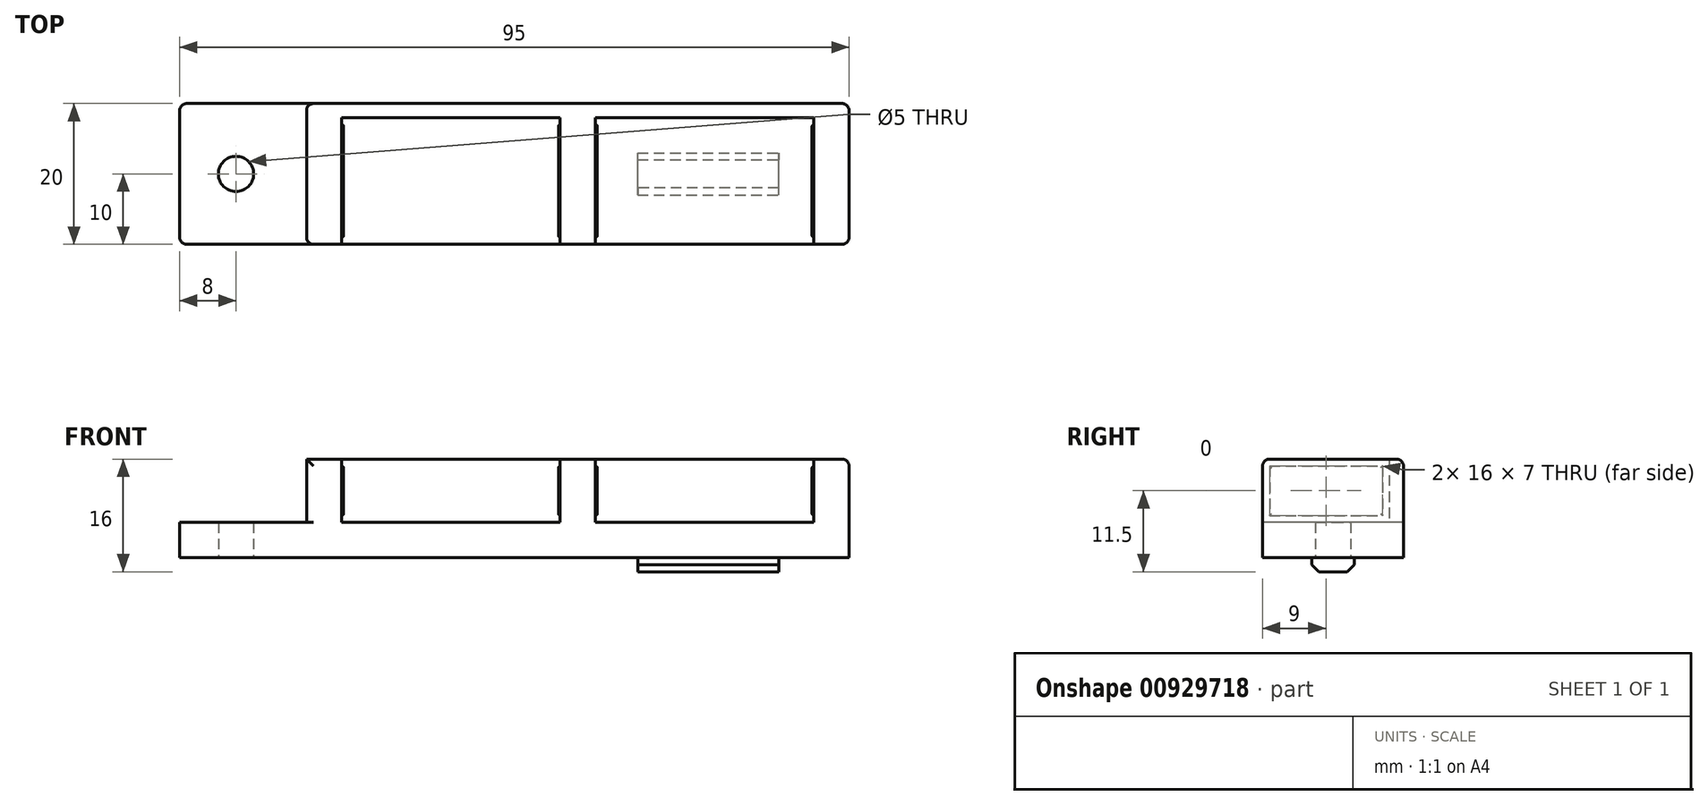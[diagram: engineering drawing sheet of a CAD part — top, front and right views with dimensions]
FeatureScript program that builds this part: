
annotation { "Feature Type Name" : "Feature", "Feature Type Description" : "" }
export const myFeature = defineFeature(function(context is Context, id is Id, definition is map)
    precondition{}
    {
        {
            var Q0;
            Q0=qCreatedBy(makeId("Top.planeOp"),FACE);
            var sketch = newSketch(context, id + "F0", { "sketchPlane" : qUnion([Q0])});
            skLineSegment(sketch, "E0.bottom", {"start": v(-47.5, 10) * mm, "end": v(47.5, 10) * mm});
            skLineSegment(sketch, "E0.top", {"start": v(-47.5, -10) * mm, "end": v(47.5, -10) * mm});
            skLineSegment(sketch, "E0.left", {"start": v(-47.5, 10) * mm, "end": v(-47.5, -10) * mm});
            skLineSegment(sketch, "E0.right", {"start": v(47.5, 10) * mm, "end": v(47.5, -10) * mm});
            skLineSegment(sketch, "E1.bottom", {"start": v(47.5, 10) * mm, "end": v(42.5, 10) * mm});
            skLineSegment(sketch, "E1.top", {"start": v(47.5, -10) * mm, "end": v(42.5, -10) * mm});
            skLineSegment(sketch, "E1.right", {"start": v(42.5, 10) * mm, "end": v(42.5, -10) * mm});
            skLineSegment(sketch, "E2.bottom", {"start": v(11.5, -10) * mm, "end": v(6.5, -10) * mm});
            skLineSegment(sketch, "E2.top", {"start": v(11.5, 10) * mm, "end": v(6.5, 10) * mm});
            skLineSegment(sketch, "E2.left", {"start": v(11.5, -10) * mm, "end": v(11.5, 10) * mm});
            skLineSegment(sketch, "E2.right", {"start": v(6.5, -10) * mm, "end": v(6.5, 10) * mm});
            skLineSegment(sketch, "E3.bottom", {"start": v(-29.5, 10) * mm, "end": v(-24.5, 10) * mm});
            skLineSegment(sketch, "E3.top", {"start": v(-29.5, -10) * mm, "end": v(-24.5, -10) * mm});
            skLineSegment(sketch, "E3.left", {"start": v(-29.5, 10) * mm, "end": v(-29.5, -10) * mm});
            skLineSegment(sketch, "E3.right", {"start": v(-24.5, 10) * mm, "end": v(-24.5, -10) * mm});
            skCircle(sketch, "E4", {"center": v(-39.5, 0) * mm, "radius": 2.5 * mm});
            skPoint(sketch, "E4.centerSnap0", {"position": v(-47.5, 0) * mm});
            skLineSegment(sketch, "E5.bottom", {"start": v(-24.5, 10) * mm, "end": v(6.5, 10) * mm});
            skLineSegment(sketch, "E5.top", {"start": v(-24.5, 8) * mm, "end": v(6.5, 8) * mm});
            skLineSegment(sketch, "E5.left", {"start": v(-24.5, 10) * mm, "end": v(-24.5, 8) * mm});
            skLineSegment(sketch, "E5.right", {"start": v(6.5, 10) * mm, "end": v(6.5, 8) * mm});
            skLineSegment(sketch, "E6.bottom", {"start": v(11.5, 10) * mm, "end": v(42.5, 10) * mm});
            skLineSegment(sketch, "E6.top", {"start": v(11.5, 8) * mm, "end": v(42.5, 8) * mm});
            skLineSegment(sketch, "E6.left", {"start": v(11.5, 10) * mm, "end": v(11.5, 8) * mm});
            skLineSegment(sketch, "E6.right", {"start": v(42.5, 10) * mm, "end": v(42.5, 8) * mm});
            skSolve(sketch);
        }
        {
            var Q0;
            {var subQ1=sQuery(id+"F0.wireOp",EDGE,"E0.left");Q0=makeQuery(id+"F0.imprint","IMPRINT",FACE,{"disambiguationData":[TD([[makeQuery(id+"F0.imprint","IMPRINT",EDGE,{"derivedFrom":subQ1}),1.0]])]});}
            var Q1;
            {var subQ4=sQuery(id+"F0.wireOp",EDGE,"E3.left");Q1=makeQuery(id+"F0.imprint","IMPRINT",FACE,{"disambiguationData":[TD([[makeQuery(id+"F0.imprint","IMPRINT",EDGE,{"derivedFrom":subQ4}),1.0]])]});}
            var Q2;
            {var subQ5=sQuery(id+"F0.wireOp",EDGE,"E5.top");Q2=makeQuery(id+"F0.imprint","IMPRINT",FACE,{"disambiguationData":[TD([[makeQuery(id+"F0.imprint","IMPRINT",EDGE,{"derivedFrom":subQ5}),-1.0]])]});}
            var Q3;
            {var subQ0=sQuery(id+"F0.wireOp",EDGE,"E2.left");var subQ1=sQuery(id+"F0.wireOp",EDGE,"E0.bottom");var subQ2=makeQuery(id+"F0.imprint","INTERSECT",VERTEX,{"derivedFrom":[subQ1,subQ0]});Q3=makeQuery(id+"F0.imprint","IMPRINT",FACE,{"disambiguationData":[TD([[makeQuery(id+"F0.imprint","IMPRINT",EDGE,{"disambiguationData":[TD([[subQ2,1.0]])],"derivedFrom":subQ1}),-1.0]])]});}
            var Q4;
            {var subQ4=sQuery(id+"F0.wireOp",EDGE,"E0.right");Q4=makeQuery(id+"F0.imprint","IMPRINT",FACE,{"disambiguationData":[TD([[makeQuery(id+"F0.imprint","IMPRINT",EDGE,{"derivedFrom":subQ4}),-1.0]])]});}
            var Q5;
            {var subQ5=sQuery(id+"F0.wireOp",EDGE,"E5.top");Q5=makeQuery(id+"F0.imprint","IMPRINT",FACE,{"disambiguationData":[TD([[makeQuery(id+"F0.imprint","IMPRINT",EDGE,{"derivedFrom":subQ5}),1.0]])]});}
            var Q6;
            {var subQ5=sQuery(id+"F0.wireOp",EDGE,"E6.top");Q6=makeQuery(id+"F0.imprint","IMPRINT",FACE,{"disambiguationData":[TD([[makeQuery(id+"F0.imprint","IMPRINT",EDGE,{"derivedFrom":subQ5}),-1.0]])]});}
            var Q7;
            {var subQ5=sQuery(id+"F0.wireOp",EDGE,"E6.top");Q7=makeQuery(id+"F0.imprint","IMPRINT",FACE,{"disambiguationData":[TD([[makeQuery(id+"F0.imprint","IMPRINT",EDGE,{"derivedFrom":subQ5}),1.0]])]});}
            extrude(context, id + "F1", {"entities" : qUnion([Q0, Q1, Q2, Q3, Q4, Q5, Q6, Q7]), "depth" : 5 * mm, "offsetDistance" : 25 * mm});
        }
        {
            var Q0;
            {var subQ4=sQuery(id+"F0.wireOp",EDGE,"E3.left");Q0=makeQuery(id+"F0.imprint","IMPRINT",FACE,{"disambiguationData":[TD([[makeQuery(id+"F0.imprint","IMPRINT",EDGE,{"derivedFrom":subQ4}),1.0]])]});}
            var Q1;
            {var subQ0=sQuery(id+"F0.wireOp",EDGE,"E2.left");var subQ1=sQuery(id+"F0.wireOp",EDGE,"E0.bottom");var subQ2=makeQuery(id+"F0.imprint","INTERSECT",VERTEX,{"derivedFrom":[subQ1,subQ0]});Q1=makeQuery(id+"F0.imprint","IMPRINT",FACE,{"disambiguationData":[TD([[makeQuery(id+"F0.imprint","IMPRINT",EDGE,{"disambiguationData":[TD([[subQ2,1.0]])],"derivedFrom":subQ1}),-1.0]])]});}
            var Q2;
            {var subQ4=sQuery(id+"F0.wireOp",EDGE,"E0.right");Q2=makeQuery(id+"F0.imprint","IMPRINT",FACE,{"disambiguationData":[TD([[makeQuery(id+"F0.imprint","IMPRINT",EDGE,{"derivedFrom":subQ4}),-1.0]])]});}
            var Q3;
            {var subQ5=sQuery(id+"F0.wireOp",EDGE,"E5.top");Q3=makeQuery(id+"F0.imprint","IMPRINT",FACE,{"disambiguationData":[TD([[makeQuery(id+"F0.imprint","IMPRINT",EDGE,{"derivedFrom":subQ5}),1.0]])]});}
            var Q4;
            {var subQ5=sQuery(id+"F0.wireOp",EDGE,"E6.top");Q4=makeQuery(id+"F0.imprint","IMPRINT",FACE,{"disambiguationData":[TD([[makeQuery(id+"F0.imprint","IMPRINT",EDGE,{"derivedFrom":subQ5}),1.0]])]});}
            extrude(context, id + "F2", {"entities" : qUnion([Q0, Q1, Q2, Q3, Q4]), "operationType" : NewBodyOperationType.ADD, "depth" : 14 * mm, "offsetDistance" : 25 * mm});
        }
        {
            var Q0;
            Q0=makeQuery(id+"F2.opExtrude","SWEPT_FACE",FACE,{"disambiguationData":[OSD([sQuery(id+"F0.wireOp",EDGE,"E3.right")])]});
            var sketch = newSketch(context, id + "F3", { "sketchPlane" : qUnion([Q0])});
            skLineSegment(sketch, "E7.bottom", {"start": v(-9, 13) * mm, "end": v(7, 13) * mm});
            skLineSegment(sketch, "E7.top", {"start": v(-9, 6) * mm, "end": v(7, 6) * mm});
            skLineSegment(sketch, "E7.left", {"start": v(-9, 13) * mm, "end": v(-9, 6) * mm});
            skLineSegment(sketch, "E7.right", {"start": v(7, 13) * mm, "end": v(7, 6) * mm});
            skSolve(sketch);
        }
        {
            var Q0;
            Q0=makeQuery(id+"F2.opExtrude","SWEPT_FACE",FACE,{"disambiguationData":[OSD([sQuery(id+"F0.wireOp",EDGE,"E2.right")])]});
            var sketch = newSketch(context, id + "F4", { "sketchPlane" : qUnion([Q0])});
            skLineSegment(sketch, "E8.bottom", {"start": v(-7, 6) * mm, "end": v(9, 6) * mm});
            skLineSegment(sketch, "E8.top", {"start": v(-7, 13) * mm, "end": v(9, 13) * mm});
            skLineSegment(sketch, "E8.left", {"start": v(-7, 6) * mm, "end": v(-7, 13) * mm});
            skLineSegment(sketch, "E8.right", {"start": v(9, 6) * mm, "end": v(9, 13) * mm});
            skSolve(sketch);
        }
        {
            var Q0;
            Q0=makeQuery(id+"F2.opExtrude","SWEPT_FACE",FACE,{"disambiguationData":[OSD([sQuery(id+"F0.wireOp",EDGE,"E2.left")])]});
            var sketch = newSketch(context, id + "F5", { "sketchPlane" : qUnion([Q0])});
            skLineSegment(sketch, "E9.bottom", {"start": v(-9, 13) * mm, "end": v(7, 13) * mm});
            skLineSegment(sketch, "E9.top", {"start": v(-9, 6) * mm, "end": v(7, 6) * mm});
            skLineSegment(sketch, "E9.left", {"start": v(-9, 13) * mm, "end": v(-9, 6) * mm});
            skLineSegment(sketch, "E9.right", {"start": v(7, 13) * mm, "end": v(7, 6) * mm});
            skSolve(sketch);
        }
        {
            var Q0;
            Q0=makeQuery(id+"F2.opExtrude","SWEPT_FACE",FACE,{"disambiguationData":[OSD([sQuery(id+"F0.wireOp",EDGE,"E1.right")])]});
            var sketch = newSketch(context, id + "F6", { "sketchPlane" : qUnion([Q0])});
            skLineSegment(sketch, "E10.bottom", {"start": v(-7, 13) * mm, "end": v(9, 13) * mm});
            skLineSegment(sketch, "E10.top", {"start": v(-7, 6) * mm, "end": v(9, 6) * mm});
            skLineSegment(sketch, "E10.left", {"start": v(-7, 13) * mm, "end": v(-7, 6) * mm});
            skLineSegment(sketch, "E10.right", {"start": v(9, 13) * mm, "end": v(9, 6) * mm});
            skSolve(sketch);
        }
        {
            var Q0;
            Q0=makeQuery(id+"F3.imprint","IMPRINT",FACE,{"disambiguationData":[TD([[makeQuery(id+"F3.imprint","IMPRINT",EDGE,{"derivedFrom":sQuery(id+"F3.wireOp",EDGE,"E7.bottom")}),-1.0]])]});
            var Q1;
            Q1=makeQuery(id+"F5.imprint","IMPRINT",FACE,{"disambiguationData":[TD([[makeQuery(id+"F5.imprint","IMPRINT",EDGE,{"derivedFrom":sQuery(id+"F5.wireOp",EDGE,"E9.bottom")}),-1.0]])]});
            extrude(context, id + "F7", {"entities" : qUnion([Q0, Q1]), "operationType" : NewBodyOperationType.ADD, "depth" : .25 * mm, "offsetDistance" : 25 * mm});
        }
        {
            var Q0;
            Q0=makeQuery(id+"F4.imprint","IMPRINT",FACE,{"disambiguationData":[TD([[makeQuery(id+"F4.imprint","IMPRINT",EDGE,{"derivedFrom":sQuery(id+"F4.wireOp",EDGE,"E8.bottom")}),1.0]])]});
            var Q1;
            Q1=makeQuery(id+"F6.imprint","IMPRINT",FACE,{"disambiguationData":[TD([[makeQuery(id+"F6.imprint","IMPRINT",EDGE,{"derivedFrom":sQuery(id+"F6.wireOp",EDGE,"E10.bottom")}),-1.0]])]});
            extrude(context, id + "F8", {"entities" : qUnion([Q0, Q1]), "operationType" : NewBodyOperationType.ADD, "depth" : .25 * mm, "offsetDistance" : 25 * mm});
        }
        {
            var Q0;
            Q0=makeQuery(id+"F7.opExtrude","CAP_FACE",FACE,{"disambiguationData":[OSD([sQuery(id+"F3.wireOp",EDGE,"E7.bottom"),sQuery(id+"F3.wireOp",EDGE,"E7.top"),sQuery(id+"F3.wireOp",EDGE,"E7.left"),sQuery(id+"F3.wireOp",EDGE,"E7.right")])],"isStart":false});
            var Q1;
            Q1=makeQuery(id+"F8.opExtrude","CAP_FACE",FACE,{"disambiguationData":[OSD([sQuery(id+"F4.wireOp",EDGE,"E8.bottom"),sQuery(id+"F4.wireOp",EDGE,"E8.top"),sQuery(id+"F4.wireOp",EDGE,"E8.left"),sQuery(id+"F4.wireOp",EDGE,"E8.right")])],"isStart":false});
            var Q2;
            Q2=makeQuery(id+"F7.opExtrude","CAP_FACE",FACE,{"disambiguationData":[OSD([sQuery(id+"F5.wireOp",EDGE,"E9.bottom"),sQuery(id+"F5.wireOp",EDGE,"E9.top"),sQuery(id+"F5.wireOp",EDGE,"E9.left"),sQuery(id+"F5.wireOp",EDGE,"E9.right")])],"isStart":false});
            var Q3;
            Q3=makeQuery(id+"F8.opExtrude","CAP_FACE",FACE,{"disambiguationData":[OSD([sQuery(id+"F6.wireOp",EDGE,"E10.bottom"),sQuery(id+"F6.wireOp",EDGE,"E10.top"),sQuery(id+"F6.wireOp",EDGE,"E10.left"),sQuery(id+"F6.wireOp",EDGE,"E10.right")])],"isStart":false});
            fillet(context, id + "F9", {"entities" : qUnion([Q0, Q1, Q2, Q3]), "radius" : .25 * mm, "tangentPropagation" : true, "allowEdgeOverflow" : false});
        }
        {
            var Q0;
            {var subQ0=sQuery(id+"F0.wireOp",EDGE,"E0.top");Q0=makeQuery(id+"F2.opExtrude","CAP_EDGE",EDGE,{"disambiguationData":[OSD([subQ0]),TDD([makeQuery(id+"F0.imprint","IMPRINT",EDGE,{"disambiguationData":[TD([[makeQuery(id+"F0.imprint","INTERSECT",VERTEX,{"derivedFrom":[subQ0,sQuery(id+"F0.wireOp",EDGE,"E3.right")]}),1.0]])],"derivedFrom":subQ0})])],"isStart":false});}
            var Q1;
            {var subQ0=sQuery(id+"F0.wireOp",EDGE,"E0.top");Q1=makeQuery(id+"F2.opExtrude","CAP_EDGE",EDGE,{"disambiguationData":[OSD([subQ0]),TDD([makeQuery(id+"F0.imprint","IMPRINT",EDGE,{"disambiguationData":[TD([[makeQuery(id+"F0.imprint","INTERSECT",VERTEX,{"derivedFrom":[subQ0,sQuery(id+"F0.wireOp",EDGE,"E2.left")]}),1.0]])],"derivedFrom":subQ0})])],"isStart":false});}
            var Q2;
            {var subQ0=sQuery(id+"F0.wireOp",EDGE,"E0.top");Q2=makeQuery(id+"F2.opExtrude","CAP_EDGE",EDGE,{"disambiguationData":[OSD([subQ0]),TDD([makeQuery(id+"F0.imprint","IMPRINT",EDGE,{"disambiguationData":[TD([[makeQuery(id+"F0.imprint","INTERSECT",VERTEX,{"derivedFrom":[subQ0,sQuery(id+"F0.wireOp",EDGE,"E0.right")]}),1.0]])],"derivedFrom":subQ0})])],"isStart":false});}
            var Q3;
            Q3=makeQuery(id+"F2.opExtrude","CAP_EDGE",EDGE,{"disambiguationData":[OSD([sQuery(id+"F0.wireOp",EDGE,"E0.bottom")])],"isStart":false});
            var Q4;
            Q4=makeQuery(id+"F1.opExtrude","SWEPT_EDGE",EDGE,{"disambiguationData":[OSD([sQuery(id+"F0.wireOp",EDGE,"E0.top"),sQuery(id+"F0.wireOp",EDGE,"E0.left")])]});
            var Q5;
            Q5=makeQuery(id+"F1.opExtrude","SWEPT_EDGE",EDGE,{"disambiguationData":[OSD([sQuery(id+"F0.wireOp",EDGE,"E0.bottom"),sQuery(id+"F0.wireOp",EDGE,"E0.left")])]});
            var Q6;
            {var subQ0=sQuery(id+"F0.wireOp",EDGE,"E0.right");var subQ1=sQuery(id+"F0.wireOp",EDGE,"E0.top");Q6=makeQuery(id+"F2.boolean.opBoolean","MERGE",EDGE,{"derivedFrom":[makeQuery(id+"F1.opExtrude","SWEPT_EDGE",EDGE,{"disambiguationData":[OSD([subQ1,subQ0])]}),makeQuery(id+"F2.opExtrude","SWEPT_EDGE",EDGE,{"disambiguationData":[OSD([subQ1,subQ0])]})]});}
            var Q7;
            {var subQ0=sQuery(id+"F0.wireOp",EDGE,"E0.right");var subQ1=sQuery(id+"F0.wireOp",EDGE,"E0.bottom");Q7=makeQuery(id+"F2.boolean.opBoolean","MERGE",EDGE,{"derivedFrom":[makeQuery(id+"F1.opExtrude","SWEPT_EDGE",EDGE,{"disambiguationData":[OSD([subQ1,subQ0])]}),makeQuery(id+"F2.opExtrude","SWEPT_EDGE",EDGE,{"disambiguationData":[OSD([subQ1,subQ0])]})]});}
            var Q8;
            Q8=makeQuery(id+"F2.opExtrude","CAP_EDGE",EDGE,{"disambiguationData":[OSD([sQuery(id+"F0.wireOp",EDGE,"E0.right")])],"isStart":false});
            var Q9;
            Q9=makeQuery(id+"F2.opExtrude","SWEPT_EDGE",EDGE,{"disambiguationData":[OSD([sQuery(id+"F0.wireOp",EDGE,"E0.top"),sQuery(id+"F0.wireOp",EDGE,"E3.left")])]});
            var Q10;
            Q10=makeQuery(id+"F2.opExtrude","SWEPT_EDGE",EDGE,{"disambiguationData":[OSD([sQuery(id+"F0.wireOp",EDGE,"E0.bottom"),sQuery(id+"F0.wireOp",EDGE,"E3.left")])]});
            fillet(context, id + "F10", {"entities" : qUnion([Q0, Q1, Q2, Q3, Q4, Q5, Q6, Q7, Q8, Q9, Q10]), "radius" : 1 * mm, "tangentPropagation" : true, "allowEdgeOverflow" : false});
        }
        {
            var Q0;
            {var subQ5=sQuery(id+"F0.wireOp",EDGE,"E6.top");Q0=makeQuery(id+"F0.imprint","IMPRINT",FACE,{"disambiguationData":[TD([[makeQuery(id+"F0.imprint","IMPRINT",EDGE,{"derivedFrom":subQ5}),-1.0]])]});}
            var sketch = newSketch(context, id + "F11", { "sketchPlane" : qUnion([Q0])});
            skLineSegment(sketch, "E11.bottom", {"start": v(17.5, -3) * mm, "end": v(37.5, -3) * mm});
            skLineSegment(sketch, "E11.top", {"start": v(17.5, 3) * mm, "end": v(37.5, 3) * mm});
            skLineSegment(sketch, "E11.left", {"start": v(17.5, -3) * mm, "end": v(17.5, 3) * mm});
            skLineSegment(sketch, "E11.right", {"start": v(37.5, -3) * mm, "end": v(37.5, 3) * mm});
            skSolve(sketch);
        }
        {
            var Q0;
            Q0=makeQuery(id+"F11.imprint","IMPRINT",FACE,{"disambiguationData":[TD([[makeQuery(id+"F11.imprint","IMPRINT",EDGE,{"derivedFrom":sQuery(id+"F11.wireOp",EDGE,"E11.bottom")}),1.0]])]});
            extrude(context, id + "F12", {"entities" : qUnion([Q0]), "operationType" : NewBodyOperationType.ADD, "oppositeDirection" : true, "depth" : 2 * mm, "offsetDistance" : 25 * mm});
        }
        {
            var Q0;
            Q0=makeQuery(id+"F12.opExtrude","CAP_EDGE",EDGE,{"disambiguationData":[OSD([sQuery(id+"F11.wireOp",EDGE,"E11.bottom")])],"isStart":false});
            var Q1;
            Q1=makeQuery(id+"F12.opExtrude","CAP_EDGE",EDGE,{"disambiguationData":[OSD([sQuery(id+"F11.wireOp",EDGE,"E11.top")])],"isStart":false});
            chamfer(context, id + "F13", {"entities" : qUnion([Q0, Q1]), "width" : 1 * mm, "tangentPropagation" : true});
        }
    });
